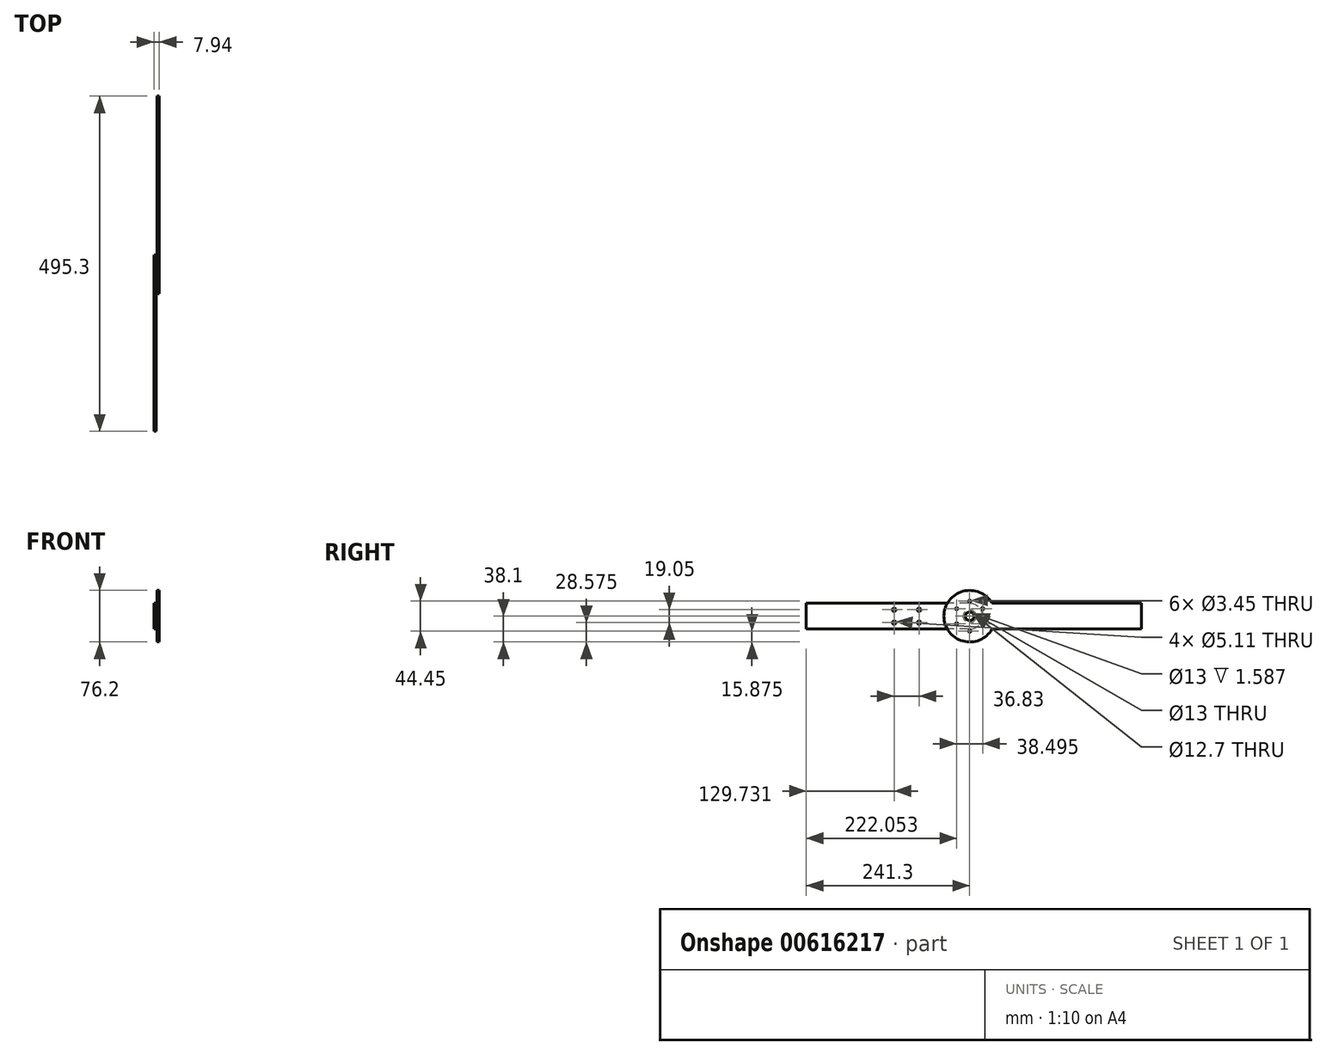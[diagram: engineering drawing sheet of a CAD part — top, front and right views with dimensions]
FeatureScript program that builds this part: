
annotation { "Feature Type Name" : "Feature", "Feature Type Description" : "" }
export const myFeature = defineFeature(function(context is Context, id is Id, definition is map)
    precondition{}
    {
        {
            var Q0;
            Q0=qCreatedBy(makeId("Right.planeOp"),FACE);
            var sketch = newSketch(context, id + "F0", { "sketchPlane" : qUnion([Q0])});
            skCircle(sketch, "E0", {"center": v(0, 0) * mm, "radius": 38.1 * mm});
            skLineSegment(sketch, "E1.bottom", {"start": v(35.92, -12.7) * mm, "end": v(254, -12.7) * mm});
            skLineSegment(sketch, "E1.top", {"start": v(35.92, 12.7) * mm, "end": v(254, 12.7) * mm});
            skLineSegment(sketch, "E1.left", {"start": v(35.92, -12.7) * mm, "end": v(35.92, 12.7) * mm});
            skLineSegment(sketch, "E1.right", {"start": v(254, -12.7) * mm, "end": v(254, 12.7) * mm});
            skCircle(sketch, "E2", {"center": v(0, 0) * mm, "radius": 6.35 * mm});
            skSolve(sketch);
        }
        {
            var Q0;
            {var subQ0=sQuery(id+"F0.wireOp",EDGE,"E1.left");Q0=makeQuery(id+"F0.imprint","IMPRINT",FACE,{"disambiguationData":[TD([[makeQuery(id+"F0.imprint","IMPRINT",EDGE,{"derivedFrom":subQ0}),1.0]])]});}
            var Q1;
            {var subQ1=sQuery(id+"F0.wireOp",EDGE,"E1.bottom");Q1=makeQuery(id+"F0.imprint","IMPRINT",FACE,{"disambiguationData":[TD([[makeQuery(id+"F0.imprint","IMPRINT",EDGE,{"derivedFrom":subQ1}),1.0]])]});}
            var Q2;
            {var subQ0=sQuery(id+"F0.wireOp",EDGE,"E1.left");Q2=makeQuery(id+"F0.imprint","IMPRINT",FACE,{"disambiguationData":[TD([[makeQuery(id+"F0.imprint","IMPRINT",EDGE,{"derivedFrom":subQ0}),-1.0]])]});}
            extrude(context, id + "F1", {"entities" : qUnion([Q0, Q1, Q2]), "depth" : 3.17 * mm});
        }
        {
            var Q0;
            Q0=makeQuery(id+"F1.opExtrude","CAP_FACE",FACE,{"disambiguationData":[OSD([sQuery(id+"F0.wireOp",EDGE,"E0"),sQuery(id+"F0.wireOp",EDGE,"E1.bottom"),sQuery(id+"F0.wireOp",EDGE,"E1.top"),sQuery(id+"F0.wireOp",EDGE,"E1.right"),sQuery(id+"F0.wireOp",EDGE,"E2")])],"isStart":true});
            var sketch = newSketch(context, id + "F2", { "sketchPlane" : qUnion([Q0])});
            skCircle(sketch, "E3", {"center": v(0, 0) * mm, "radius": 9.53 * mm});
            skCircle(sketch, "E4", {"center": v(0, 0) * mm, "radius": 6.5 * mm});
            skSolve(sketch);
        }
        {
            var Q0;
            Q0=qSketchRegion(id+"F2",true);
            extrude(context, id + "F3", {"entities" : qUnion([Q0]), "depth" : 1.59 * mm});
        }
        {
            var Q0;
            Q0=makeQuery(id+"F1.opExtrude","CAP_FACE",FACE,{"disambiguationData":[OSD([sQuery(id+"F0.wireOp",EDGE,"E0"),sQuery(id+"F0.wireOp",EDGE,"E1.bottom"),sQuery(id+"F0.wireOp",EDGE,"E1.top"),sQuery(id+"F0.wireOp",EDGE,"E1.right"),sQuery(id+"F0.wireOp",EDGE,"E2")])],"isStart":false});
            var sketch = newSketch(context, id + "F4", { "sketchPlane" : qUnion([Q0])});
            skArc(sketch, "E5.0.0", {"start": v(35.92, 12.7) * mm, "mid": v(-38.1, 0) * mm, "end": v(35.92, -12.7) * mm});
            skLineSegment(sketch, "E5.0.1", {"start": v(35.92, -12.7) * mm, "end": v(254, -12.7) * mm});
            skLineSegment(sketch, "E5.0.2", {"start": v(254, -12.7) * mm, "end": v(254, 12.7) * mm});
            skLineSegment(sketch, "E5.0.3", {"start": v(254, 12.7) * mm, "end": v(35.92, 12.7) * mm});
            skCircle(sketch, "E6", {"center": v(0, 0) * mm, "radius": 22.23 * mm, "construction": true});
            skPoint(sketch, "E7", {"position": v(0, 22.23) * mm});
            skPoint(sketch, "E8.1.0", {"position": v(-19.25, 11.11) * mm});
            skPoint(sketch, "E8.2.0", {"position": v(-19.25, -11.11) * mm});
            skPoint(sketch, "E9.0.3.0", {"position": v(0, -22.23) * mm});
            skPoint(sketch, "E10.0.4.0", {"position": v(19.25, -11.11) * mm});
            skPoint(sketch, "E10.0.5.0", {"position": v(19.25, 11.11) * mm});
            skSolve(sketch);
        }
        {
            var Q0;
            Q0=sQuery(id+"F4.wireOp",VERTEX,"E7");
            var Q1;
            Q1=sQuery(id+"F4.wireOp",VERTEX,"E8.2.0");
            var Q2;
            Q2=sQuery(id+"F4.wireOp",VERTEX,"E8.1.0");
            var Q3;
            Q3=sQuery(id+"F4.wireOp",VERTEX,"E9.0.3.0");
            var Q4;
            Q4=sQuery(id+"F4.wireOp",VERTEX,"E10.0.5.0");
            var Q5;
            Q5=sQuery(id+"F4.wireOp",VERTEX,"E10.0.4.0");
            var Q6;
            Q6=makeQuery(id+"F1.opExtrude","SWEPT_BODY",BODY,{"disambiguationData":[OSD([sQuery(id+"F0.wireOp",EDGE,"E0"),sQuery(id+"F0.wireOp",EDGE,"E1.bottom"),sQuery(id+"F0.wireOp",EDGE,"E1.top"),sQuery(id+"F0.wireOp",EDGE,"E1.right"),sQuery(id+"F0.wireOp",EDGE,"E2")])]});
            hole(context, id + "F5", {"style" : HoleStyle.SIMPLE, "endStyle" : HoleEndStyle.THROUGH, "standardTappedOrClearance" : lookupTablePath({ "standard" : "ANSI", "engagement" : "75%", "pitch" : "32 tpi", "size" : "#8", "type" : "Tapped" }), "standardBlindInLast" : lookupTablePath({ "standard" : "ANSI", "engagement" : "75%", "pitch" : "32 tpi", "size" : "#8", "type" : "Tapped" }), "holeDiameter" : 3.45 * mm, "locations" : qUnion([Q0, Q1, Q2, Q3, Q4, Q5]), "scope" : qUnion([Q6]), "isTappedThrough" : true, "majorDiameter" : 4.17 * mm, "showTappedDepth" : true});
        }
        {
            var Q0;
            Q0=makeQuery(id+"F3.opExtrude","CAP_FACE",FACE,{"disambiguationData":[OSD([sQuery(id+"F2.wireOp",EDGE,"E3"),sQuery(id+"F2.wireOp",EDGE,"E4")])],"isStart":false});
            var sketch = newSketch(context, id + "F6", { "sketchPlane" : qUnion([Q0])});
            skLineSegment(sketch, "E11.bottom", {"start": v(0, 19.05) * mm, "end": v(241.3, 19.05) * mm});
            skLineSegment(sketch, "E11.top", {"start": v(0, -19.05) * mm, "end": v(241.3, -19.05) * mm});
            skLineSegment(sketch, "E11.left", {"start": v(-19.05, 0) * mm, "end": v(-19.05, 0) * mm});
            skLineSegment(sketch, "E11.right", {"start": v(241.3, 19.05) * mm, "end": v(241.3, -19.05) * mm});
            skPoint(sketch, "E12.visualSharp", {"position": v(-19.05, 19.05) * mm});
            skArc(sketch, "E12.filletArc", {"start": v(0, 19.05) * mm, "mid": v(-13.47, 13.47) * mm, "end": v(-19.05, 0) * mm});
            skPoint(sketch, "E13.visualSharp", {"position": v(-19.05, -19.05) * mm});
            skArc(sketch, "E13.filletArc", {"start": v(-19.05, 0) * mm, "mid": v(-13.47, -13.47) * mm, "end": v(0, -19.05) * mm});
            skCircle(sketch, "E14", {"center": v(0, 0) * mm, "radius": 6.35 * mm});
            skPoint(sketch, "E15", {"position": v(74.74, 9.52) * mm});
            skPoint(sketch, "E16", {"position": v(74.74, -9.53) * mm});
            skPoint(sketch, "E17", {"position": v(111.57, -9.53) * mm});
            skPoint(sketch, "E18", {"position": v(111.57, 9.52) * mm});
            skLineSegment(sketch, "E19", {"start": v(115.38, 19.05) * mm, "end": v(115.38, -19.05) * mm, "construction": true});
            skSolve(sketch);
        }
        {
            var Q0;
            Q0=makeQuery(id+"F6.imprint","IMPRINT",FACE,{"disambiguationData":[TD([[makeQuery(id+"F6.imprint","IMPRINT",EDGE,{"derivedFrom":sQuery(id+"F6.wireOp",EDGE,"E11.bottom")}),-1.0]])]});
            var Q1;
            Q1=makeQuery(id+"F6.imprint","IMPRINT",FACE,{"disambiguationData":[TD([[makeQuery(id+"F6.imprint","IMPRINT",EDGE,{"derivedFrom":makeQuery(id+"F3.opExtrude","CAP_EDGE",EDGE,{"disambiguationData":[OSD([sQuery(id+"F2.wireOp",EDGE,"E3")])],"isStart":false})}),1.0]])]});
            extrude(context, id + "F7", {"entities" : qUnion([Q0, Q1]), "depth" : 3.17 * mm});
        }
        {
            var Q0;
            Q0=sQuery(id+"F6.wireOp",VERTEX,"E18");
            var Q1;
            Q1=sQuery(id+"F6.wireOp",VERTEX,"E15");
            var Q2;
            Q2=sQuery(id+"F6.wireOp",VERTEX,"E16");
            var Q3;
            Q3=sQuery(id+"F6.wireOp",VERTEX,"E17");
            var Q4;
            Q4=makeQuery(id+"F7.opExtrude","SWEPT_BODY",BODY,{"disambiguationData":[OSD([sQuery(id+"F2.wireOp",EDGE,"E4"),sQuery(id+"F6.wireOp",EDGE,"E11.bottom"),sQuery(id+"F6.wireOp",EDGE,"E11.top"),sQuery(id+"F6.wireOp",EDGE,"E11.right"),sQuery(id+"F6.wireOp",EDGE,"E12.filletArc"),sQuery(id+"F6.wireOp",EDGE,"E13.filletArc")])]});
            hole(context, id + "F8", {"style" : HoleStyle.SIMPLE, "endStyle" : HoleEndStyle.THROUGH, "oppositeDirection" : true, "standardTappedOrClearance" : lookupTablePath({ "standard" : "ANSI", "fit" : "Normal (ASME)", "size" : "#10", "type" : "Clearance" }), "standardBlindInLast" : lookupTablePath({ "fit" : "Free", "standard" : "ANSI", "size" : "#10", "type" : "Clearance" }), "holeDiameter" : 5.1 * mm, "locations" : qUnion([Q0, Q1, Q2, Q3]), "scope" : qUnion([Q4]), "isTappedThrough" : true});
        }
        {
            var Q0;
            Q0=makeQuery(id+"F1.opExtrude","CAP_FACE",FACE,{"disambiguationData":[OSD([sQuery(id+"F0.wireOp",EDGE,"E0"),sQuery(id+"F0.wireOp",EDGE,"E1.bottom"),sQuery(id+"F0.wireOp",EDGE,"E1.top"),sQuery(id+"F0.wireOp",EDGE,"E1.right"),sQuery(id+"F0.wireOp",EDGE,"E2")])],"isStart":true});
            var sketch = newSketch(context, id + "F9", { "sketchPlane" : qUnion([Q0])});
            skLineSegment(sketch, "E20", {"start": v(-254, 12.7) * mm, "end": v(-254, 19.05) * mm});
            skLineSegment(sketch, "E21", {"start": v(-254, 19.05) * mm, "end": v(-33, 19.05) * mm});
            skLineSegment(sketch, "E22.0", {"start": v(-35.92, 12.7) * mm, "end": v(-254, 12.7) * mm});
            skArc(sketch, "E23.0", {"start": v(-35.92, 12.7) * mm, "mid": v(-34.6, 15.94) * mm, "end": v(-33, 19.05) * mm});
            skPoint(sketch, "E24.orphan", {"position": v(-35.92, -12.7) * mm});
            skLineSegment(sketch, "E25", {"start": v(-254, -12.7) * mm, "end": v(-254, -19.05) * mm});
            skLineSegment(sketch, "E26", {"start": v(-254, -19.05) * mm, "end": v(-33, -19.05) * mm});
            skLineSegment(sketch, "E27.0", {"start": v(-35.92, -12.7) * mm, "end": v(-254, -12.7) * mm});
            skSolve(sketch);
        }
        {
            var Q0;
            Q0=makeQuery(id+"F9.imprint","IMPRINT",FACE,{"disambiguationData":[TD([[makeQuery(id+"F9.imprint","IMPRINT",EDGE,{"derivedFrom":sQuery(id+"F9.wireOp",EDGE,"E20")}),-1.0]])]});
            var Q1;
            Q1=makeQuery(id+"F9.imprint","IMPRINT",FACE,{"disambiguationData":[TD([[makeQuery(id+"F9.imprint","IMPRINT",EDGE,{"derivedFrom":sQuery(id+"F9.wireOp",EDGE,"E25")}),1.0]])]});
            extrude(context, id + "F10", {"entities" : qUnion([Q0, Q1]), "operationType" : NewBodyOperationType.ADD, "oppositeDirection" : true, "depth" : 3.17 * mm});
        }
    });
